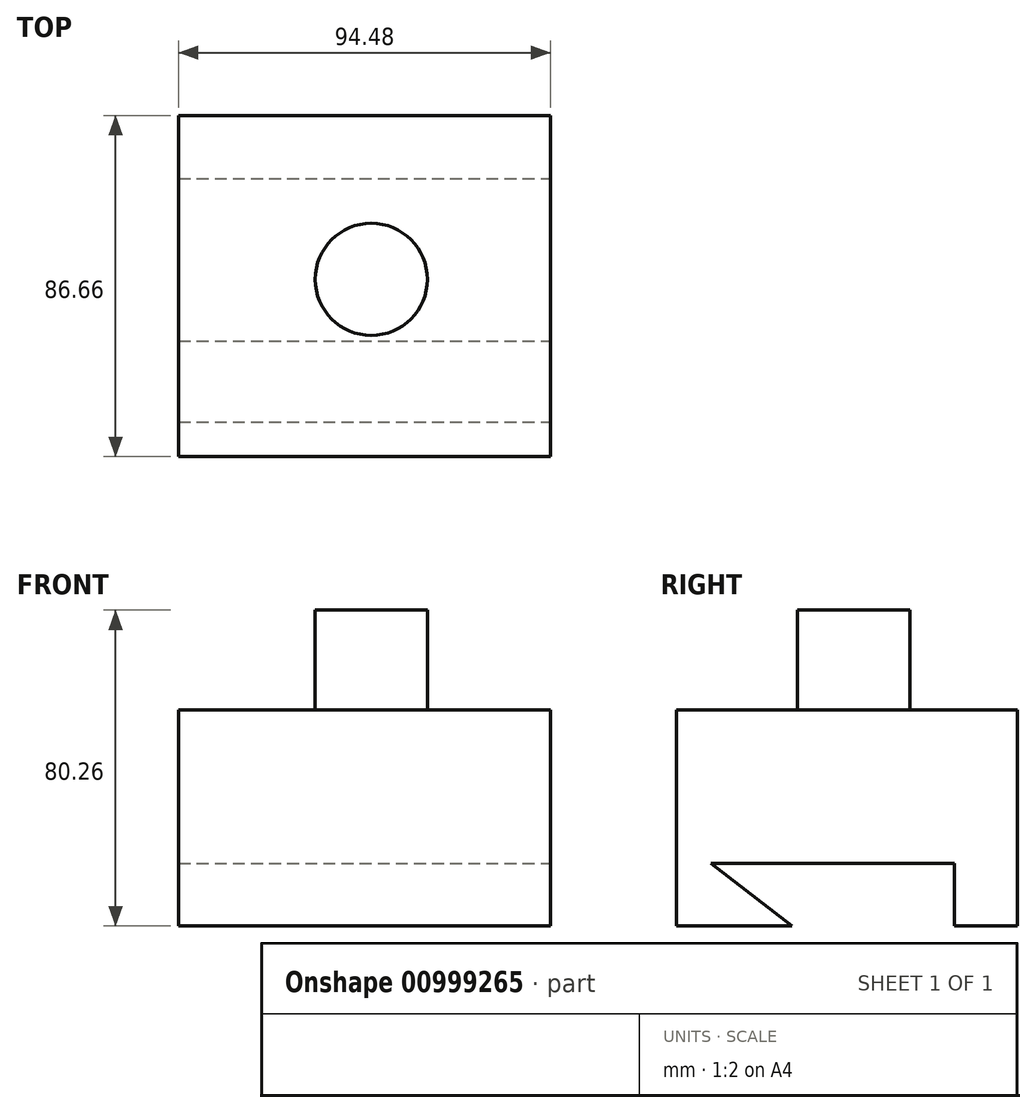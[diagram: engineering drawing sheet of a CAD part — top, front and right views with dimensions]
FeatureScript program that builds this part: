
annotation { "Feature Type Name" : "Feature", "Feature Type Description" : "" }
export const myFeature = defineFeature(function(context is Context, id is Id, definition is map)
    precondition{}
    {
        {
            var Q0;
            Q0=qCreatedBy(makeId("Top.planeOp"),FACE);
            var sketch = newSketch(context, id + "F0", { "sketchPlane" : qUnion([Q0])});
            skLineSegment(sketch, "E0.bottom", {"start": v(-48.95, -45.03) * mm, "end": v(45.53, -45.03) * mm});
            skLineSegment(sketch, "E0.top", {"start": v(-48.95, 41.63) * mm, "end": v(45.53, 41.63) * mm});
            skLineSegment(sketch, "E0.left", {"start": v(-48.95, -45.03) * mm, "end": v(-48.95, 41.63) * mm});
            skLineSegment(sketch, "E0.right", {"start": v(45.53, -45.03) * mm, "end": v(45.53, 41.63) * mm});
            skSolve(sketch);
        }
        {
            var Q0;
            Q0=makeQuery(id+"F0.imprint","IMPRINT",FACE,{"disambiguationData":[TD([[makeQuery(id+"F0.imprint","IMPRINT",EDGE,{"derivedFrom":sQuery(id+"F0.wireOp",EDGE,"E0.bottom")}),1.0]])]});
            extrude(context, id + "F1", {"entities" : qUnion([Q0]), "depth" : 54.86 * mm, "offsetDistance" : 25.4 * mm});
        }
        {
            var Q0;
            Q0=makeQuery(id+"F1.opExtrude","SWEPT_FACE",FACE,{"disambiguationData":[OSD([sQuery(id+"F0.wireOp",EDGE,"E0.right")])]});
            var sketch = newSketch(context, id + "F2", { "sketchPlane" : qUnion([Q0])});
            skLineSegment(sketch, "E1", {"start": v(-15.7, 0) * mm, "end": v(-36.26, 15.9) * mm});
            skLineSegment(sketch, "E2", {"start": v(-36.26, 15.9) * mm, "end": v(25.6, 15.9) * mm});
            skLineSegment(sketch, "E3", {"start": v(25.6, 15.9) * mm, "end": v(25.6, 0) * mm});
            skLineSegment(sketch, "E4", {"start": v(25.6, 0) * mm, "end": v(-15.7, 0) * mm});
            skSolve(sketch);
        }
        {
            var Q0;
            Q0 = qSketchRegion(id + "F2", true);
            extrude(context, id + "F3", {"entities" : qUnion([Q0]), "operationType" : NewBodyOperationType.REMOVE, "endBound" : BoundingType.THROUGH_ALL, "oppositeDirection" : true, "depth" : 25.4 * mm, "offsetDistance" : 25.4 * mm});
        }
        {
            var Q0;
            Q0=makeQuery(id+"F1.opExtrude","CAP_FACE",FACE,{"disambiguationData":[OSD([sQuery(id+"F0.wireOp",EDGE,"E0.bottom"),sQuery(id+"F0.wireOp",EDGE,"E0.top"),sQuery(id+"F0.wireOp",EDGE,"E0.left"),sQuery(id+"F0.wireOp",EDGE,"E0.right")])],"isStart":false});
            var sketch = newSketch(context, id + "F4", { "sketchPlane" : qUnion([Q0])});
            skCircle(sketch, "E5", {"center": v(0, 0) * mm, "radius": 14.24 * mm});
            skSolve(sketch);
        }
        {
            var Q0;
            Q0 = qSketchRegion(id + "F4", true);
            extrude(context, id + "F5", {"entities" : qUnion([Q0]), "operationType" : NewBodyOperationType.ADD, "depth" : 25.4 * mm, "offsetDistance" : 25.4 * mm});
        }
    });
